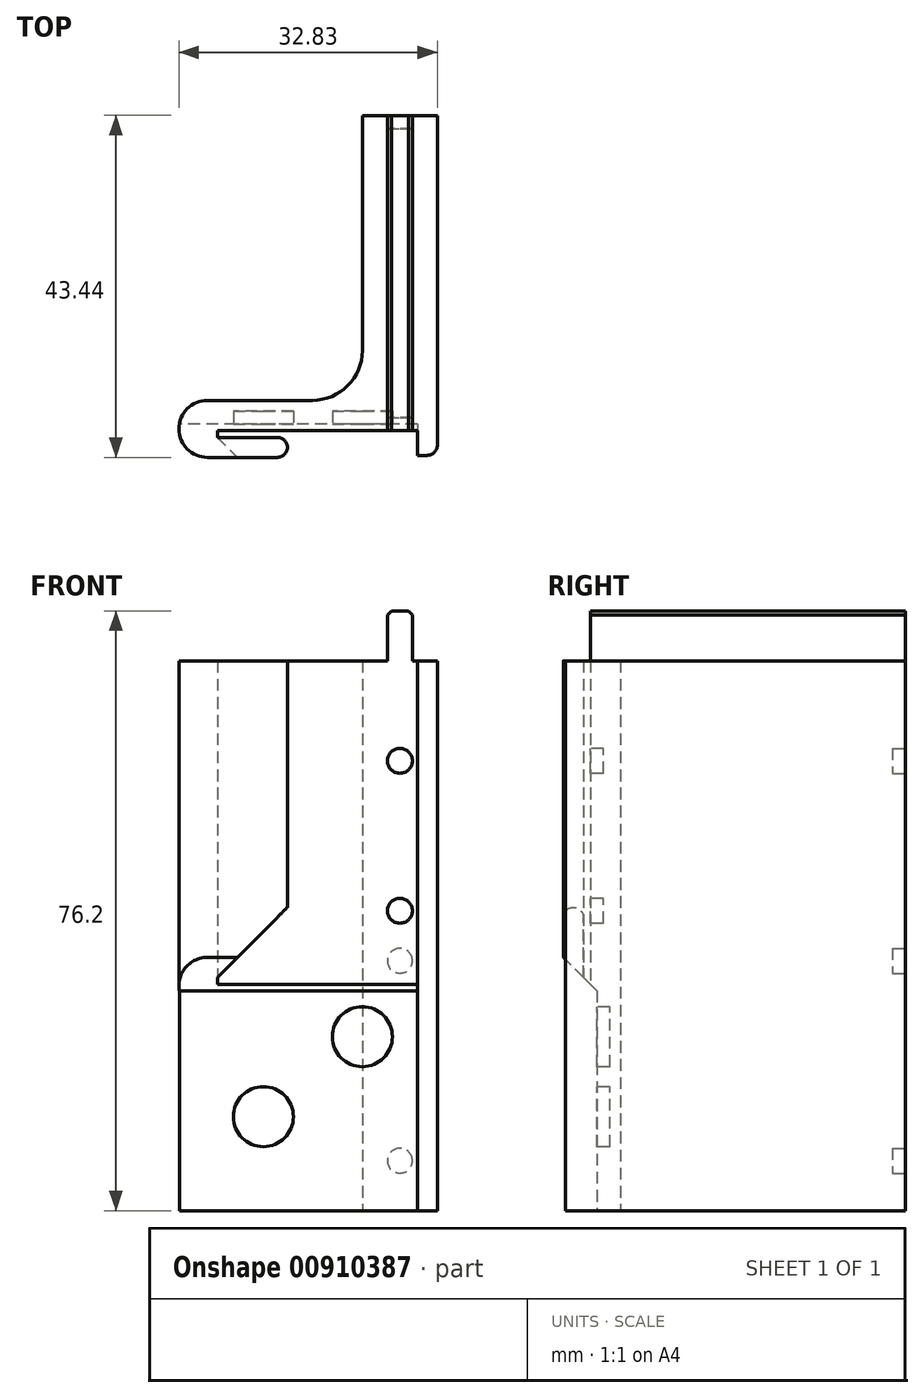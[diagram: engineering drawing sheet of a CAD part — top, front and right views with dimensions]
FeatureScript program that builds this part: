
annotation { "Feature Type Name" : "Feature", "Feature Type Description" : "" }
export const myFeature = defineFeature(function(context is Context, id is Id, definition is map)
    precondition{}
    {
        {
            var Q0;
            Q0=qCreatedBy(makeId("Top.planeOp"),FACE);
            var sketch = newSketch(context, id + "F0", { "sketchPlane" : qUnion([Q0])});
            skLineSegment(sketch, "E0", {"start": v(-6.99, 40) * mm, "end": v(-6.99, 10.16) * mm});
            skLineSegment(sketch, "E1", {"start": v(-13.34, 3.8) * mm, "end": v(-26.67, 3.8) * mm});
            skLineSegment(sketch, "E2", {"start": v(-26.67, -3.43) * mm, "end": v(-17.78, -3.43) * mm});
            skLineSegment(sketch, "E3", {"start": v(-17.78, -0.89) * mm, "end": v(-25.4, -0.89) * mm});
            skLineSegment(sketch, "E4", {"start": v(-25.4, -0.89) * mm, "end": v(-25.4, 0) * mm});
            skLineSegment(sketch, "E5", {"start": v(-25.4, 0) * mm, "end": v(0, 0) * mm});
            skLineSegment(sketch, "E6", {"start": v(0, 0) * mm, "end": v(0, -3.18) * mm});
            skLineSegment(sketch, "E7", {"start": v(0, -3.18) * mm, "end": v(1.22, -3.18) * mm});
            skLineSegment(sketch, "E8", {"start": v(2.54, -1.85) * mm, "end": v(2.54, 40) * mm});
            skLineSegment(sketch, "E9", {"start": v(2.54, 40) * mm, "end": v(-6.99, 40) * mm});
            skArc(sketch, "E10", {"start": v(-26.67, 3.8) * mm, "mid": v(-30.29, 0.2) * mm, "end": v(-26.67, -3.43) * mm});
            skPoint(sketch, "E11.visualSharp", {"position": v(-6.99, 3.81) * mm});
            skArc(sketch, "E11.filletArc", {"start": v(-13.34, 3.8) * mm, "mid": v(-8.84, 5.67) * mm, "end": v(-6.99, 10.16) * mm});
            skPoint(sketch, "E12.visualSharp", {"position": v(2.54, -3.18) * mm});
            skArc(sketch, "E12.filletArc", {"start": v(1.22, -3.18) * mm, "mid": v(2.15, -2.79) * mm, "end": v(2.54, -1.85) * mm});
            skArc(sketch, "E13", {"start": v(-17.78, -3.43) * mm, "mid": v(-16.51, -2.16) * mm, "end": v(-17.78, -0.89) * mm});
            skSolve(sketch);
        }
        {
            var Q0;
            Q0=qSketchRegion(id+"F0",true);
            extrude(context, id + "F1", {"entities" : qUnion([Q0]), "depth" : 69.85 * mm, "offsetDistance" : 25.4 * mm});
        }
        {
            var Q0;
            Q0=makeQuery(id+"F1.opExtrude","SWEPT_FACE",FACE,{"disambiguationData":[OSD([sQuery(id+"F0.wireOp",EDGE,"E9")])]});
            var sketch = newSketch(context, id + "F2", { "sketchPlane" : qUnion([Q0])});
            skLineSegment(sketch, "E14.bottom", {"start": v(3.81, 69.85) * mm, "end": v(0.64, 69.85) * mm});
            skLineSegment(sketch, "E14.top", {"start": v(3.81, 76.2) * mm, "end": v(0.64, 76.2) * mm});
            skLineSegment(sketch, "E14.left", {"start": v(3.81, 69.85) * mm, "end": v(3.81, 76.2) * mm});
            skLineSegment(sketch, "E14.right", {"start": v(0.64, 69.85) * mm, "end": v(0.64, 76.2) * mm});
            skLineSegment(sketch, "E15", {"start": v(2.22, 69.85) * mm, "end": v(2.22, 0) * mm, "construction": true});
            skSolve(sketch);
        }
        {
            var Q0;
            Q0=qSketchRegion(id+"F2",true);
            var Q1;
            Q1=makeQuery(id+"F1.opExtrude","SWEPT_FACE",FACE,{"disambiguationData":[OSD([sQuery(id+"F0.wireOp",EDGE,"E5")])]});
            extrude(context, id + "F3", {"entities" : qUnion([Q0]), "operationType" : NewBodyOperationType.ADD, "endBound" : BoundingType.UP_TO_SURFACE, "oppositeDirection" : true, "depth" : 25.4 * mm, "endBoundEntityFace" : qUnion([Q1]), "offsetDistance" : 25.4 * mm});
        }
        {
            var Q0;
            Q0=makeQuery(id+"FGGUkSzP3J2FlrJ_1.boolean.opBoolean","COPY",EDGE,{"derivedFrom":makeQuery(id+"FGGUkSzP3J2FlrJ_1.opExtrude","SWEPT_EDGE",EDGE,{"disambiguationData":[OSD([sQuery(id+"F0.wireOp",EDGE,"E9"),sQuery(id+"FaeWGxnTma6XmSR_1.wireOp",EDGE,"7cqQJsnl-rrB4-1SHC-6Jgg-oraov4HQkfV0.bottom"),sQuery(id+"FaeWGxnTma6XmSR_1.wireOp",EDGE,"7cqQJsnl-rrB4-1SHC-6Jgg-oraov4HQkfV0.right")])]})});
            var Q1;
            Q1=makeQuery(id+"FGGUkSzP3J2FlrJ_1.boolean.opBoolean","COPY",EDGE,{"derivedFrom":makeQuery(id+"FGGUkSzP3J2FlrJ_1.opExtrude","SWEPT_EDGE",EDGE,{"disambiguationData":[OSD([sQuery(id+"F0.wireOp",EDGE,"E9"),sQuery(id+"FaeWGxnTma6XmSR_1.wireOp",EDGE,"7cqQJsnl-rrB4-1SHC-6Jgg-oraov4HQkfV0.bottom"),sQuery(id+"FaeWGxnTma6XmSR_1.wireOp",EDGE,"7cqQJsnl-rrB4-1SHC-6Jgg-oraov4HQkfV0.left")])]})});
            var Q2;
            Q2=makeQuery(id+"F3.opExtrude","SWEPT_EDGE",EDGE,{"disambiguationData":[OSD([sQuery(id+"F2.wireOp",EDGE,"E14.top"),sQuery(id+"F2.wireOp",EDGE,"E14.right")])]});
            var Q3;
            Q3=makeQuery(id+"F3.opExtrude","SWEPT_EDGE",EDGE,{"disambiguationData":[OSD([sQuery(id+"F2.wireOp",EDGE,"E14.top"),sQuery(id+"F2.wireOp",EDGE,"E14.left")])]});
            chamfer(context, id + "F4", {"entities" : qUnion([Q0, Q1, Q2, Q3]), "width" : 0.5 * mm, "tangentPropagation" : true});
        }
        {
            var Q0;
            Q0=makeQuery(id+"F3.boolean.opBoolean","MERGE",FACE,{"derivedFrom":[makeQuery(id+"F1.opExtrude","SWEPT_FACE",FACE,{"disambiguationData":[OSD([sQuery(id+"F0.wireOp",EDGE,"E9")])]}),makeQuery(id+"F3.opExtrude","CAP_FACE",FACE,{"disambiguationData":[OSD([sQuery(id+"F2.wireOp",EDGE,"E14.bottom"),sQuery(id+"F2.wireOp",EDGE,"E14.top"),sQuery(id+"F2.wireOp",EDGE,"E14.left"),sQuery(id+"F2.wireOp",EDGE,"E14.right")])],"isStart":true})]});
            var sketch = newSketch(context, id + "F5", { "sketchPlane" : qUnion([Q0])});
            skCircle(sketch, "E16", {"center": v(2.22, 6.35) * mm, "radius": 1.59 * mm});
            skCircle(sketch, "E17", {"center": v(2.22, 31.75) * mm, "radius": 1.59 * mm});
            skCircle(sketch, "E18", {"center": v(2.22, 57.15) * mm, "radius": 1.59 * mm});
            skLineSegment(sketch, "E19", {"start": v(2.22, 0) * mm, "end": v(2.22, 6.35) * mm, "construction": true});
            skLineSegment(sketch, "E20", {"start": v(2.22, 31.75) * mm, "end": v(2.22, 6.35) * mm, "construction": true});
            skLineSegment(sketch, "E21", {"start": v(2.22, 57.15) * mm, "end": v(2.22, 31.75) * mm, "construction": true});
            skLineSegment(sketch, "E22", {"start": v(2.22, 57.15) * mm, "end": v(2.22, 69.85) * mm, "construction": true});
            skSolve(sketch);
        }
        {
            var Q0;
            Q0=qSketchRegion(id+"F5",true);
            extrude(context, id + "F6", {"entities" : qUnion([Q0]), "operationType" : NewBodyOperationType.REMOVE, "oppositeDirection" : true, "depth" : 1.65 * mm, "offsetDistance" : 25.4 * mm});
        }
        {
            var Q0;
            Q0=makeQuery(id+"F3.boolean.opBoolean","MERGE",FACE,{"derivedFrom":[makeQuery(id+"F1.opExtrude","SWEPT_FACE",FACE,{"disambiguationData":[OSD([sQuery(id+"F0.wireOp",EDGE,"E5")])]}),makeQuery(id+"F3.opExtrude","CAP_FACE",FACE,{"disambiguationData":[OSD([sQuery(id+"F2.wireOp",EDGE,"E14.bottom"),sQuery(id+"F2.wireOp",EDGE,"E14.top"),sQuery(id+"F2.wireOp",EDGE,"E14.left"),sQuery(id+"F2.wireOp",EDGE,"E14.right")])],"isStart":false})]});
            var sketch = newSketch(context, id + "F7", { "sketchPlane" : qUnion([Q0])});
            skCircle(sketch, "E23.2.0", {"center": v(-2.22, 57.15) * mm, "radius": 1.59 * mm});
            skCircle(sketch, "E24", {"center": v(-2.22, 38.1) * mm, "radius": 1.59 * mm});
            skLineSegment(sketch, "E25", {"start": v(-2.22, 57.15) * mm, "end": v(-2.22, 38.1) * mm, "construction": true});
            skSolve(sketch);
        }
        {
            var Q0;
            Q0=qSketchRegion(id+"F7",true);
            extrude(context, id + "F8", {"entities" : qUnion([Q0]), "operationType" : NewBodyOperationType.REMOVE, "oppositeDirection" : true, "depth" : 1.65 * mm, "offsetDistance" : 25.4 * mm});
        }
        {
            var Q0;
            Q0=makeQuery(id+"F1.opExtrude","CAP_FACE",FACE,{"disambiguationData":[OSD([sQuery(id+"F0.wireOp",EDGE,"E0"),sQuery(id+"F0.wireOp",EDGE,"E1"),sQuery(id+"F0.wireOp",EDGE,"E2"),sQuery(id+"F0.wireOp",EDGE,"E3"),sQuery(id+"F0.wireOp",EDGE,"E4"),sQuery(id+"F0.wireOp",EDGE,"E5"),sQuery(id+"F0.wireOp",EDGE,"E6"),sQuery(id+"F0.wireOp",EDGE,"E7"),sQuery(id+"F0.wireOp",EDGE,"E8"),sQuery(id+"F0.wireOp",EDGE,"E9"),sQuery(id+"F0.wireOp",EDGE,"E10"),sQuery(id+"F0.wireOp",EDGE,"E11.filletArc"),sQuery(id+"F0.wireOp",EDGE,"E12.filletArc"),sQuery(id+"F0.wireOp",EDGE,"E13")])],"isStart":true});
            var sketch = newSketch(context, id + "F9", { "sketchPlane" : qUnion([Q0])});
            skLineSegment(sketch, "E26.bottom", {"start": v(0, -0.81) * mm, "end": v(-30.29, -0.81) * mm});
            skLineSegment(sketch, "E26.top", {"start": v(0, 3.43) * mm, "end": v(-30.29, 3.43) * mm});
            skLineSegment(sketch, "E26.left", {"start": v(0, -0.81) * mm, "end": v(0, 3.43) * mm});
            skLineSegment(sketch, "E26.right", {"start": v(-30.29, -0.81) * mm, "end": v(-30.29, 3.43) * mm});
            skSolve(sketch);
        }
        {
            var Q0;
            Q0 = qSketchRegion(id + "F9", true);
            extrude(context, id + "F10", {"entities" : qUnion([Q0]), "operationType" : NewBodyOperationType.REMOVE, "oppositeDirection" : true, "depth" : 27.94 * mm, "offsetDistance" : 25.4 * mm});
        }
        {
            var Q0;
            Q0=makeQuery(id+"F10.boolean.opBoolean","COPY",FACE,{"derivedFrom":makeQuery(id+"F10.opExtrude","SWEPT_FACE",FACE,{"disambiguationData":[OSD([sQuery(id+"F9.wireOp",EDGE,"E26.bottom")])]})});
            var sketch = newSketch(context, id + "F11", { "sketchPlane" : qUnion([Q0])});
            skCircle(sketch, "E27", {"center": v(-6.99, 22.1) * mm, "radius": 3.81 * mm});
            skCircle(sketch, "E28", {"center": v(-19.56, 11.94) * mm, "radius": 3.81 * mm});
            skSolve(sketch);
        }
        {
            var Q0;
            Q0 = qSketchRegion(id + "F11", true);
            extrude(context, id + "F12", {"entities" : qUnion([Q0]), "operationType" : NewBodyOperationType.REMOVE, "oppositeDirection" : true, "depth" : 1.65 * mm, "offsetDistance" : 25.4 * mm});
        }
        {
            var Q0;
            Q0=makeQuery(id+"F10.boolean.opBoolean","MERGE",FACE,{"derivedFrom":[makeQuery(id+"F1.opExtrude","SWEPT_FACE",FACE,{"disambiguationData":[OSD([sQuery(id+"F0.wireOp",EDGE,"E6")])]})],"fromTools":[makeQuery(id+"F10.opExtrude","SWEPT_FACE",FACE,{"disambiguationData":[OSD([sQuery(id+"F9.wireOp",EDGE,"E26.left")])]})]});
            var sketch = newSketch(context, id + "F13", { "sketchPlane" : qUnion([Q0])});
            skLineSegment(sketch, "E29", {"start": v(-0.81, 27.94) * mm, "end": v(3.43, 32.18) * mm});
            skLineSegment(sketch, "E30", {"start": v(3.43, 27.94) * mm, "end": v(-0.81, 27.94) * mm});
            skLineSegment(sketch, "E31", {"start": v(3.43, 32.18) * mm, "end": v(3.43, 27.94) * mm});
            skSolve(sketch);
        }
        {
            var Q0;
            Q0 = qSketchRegion(id + "F13", true);
            extrude(context, id + "F14", {"entities" : qUnion([Q0]), "operationType" : NewBodyOperationType.REMOVE, "endBound" : BoundingType.THROUGH_ALL, "depth" : 25.4 * mm, "offsetDistance" : 25.4 * mm});
        }
        {
            var Q0;
            Q0=makeQuery(id+"F1.opExtrude","SWEPT_FACE",FACE,{"disambiguationData":[OSD([sQuery(id+"F0.wireOp",EDGE,"E2")])]});
            var sketch = newSketch(context, id + "F15", { "sketchPlane" : qUnion([Q0])});
            skLineSegment(sketch, "E32", {"start": v(-25.4, 29.64) * mm, "end": v(-12.7, 29.64) * mm});
            skLineSegment(sketch, "E33", {"start": v(-12.7, 29.64) * mm, "end": v(-12.7, 42.34) * mm});
            skLineSegment(sketch, "E34", {"start": v(-12.7, 42.34) * mm, "end": v(-25.4, 29.64) * mm});
            skSolve(sketch);
        }
        {
            var Q0;
            Q0 = qSketchRegion(id + "F15", true);
            var Q1;
            Q1=makeQuery(id+"F1.opExtrude","SWEPT_FACE",FACE,{"disambiguationData":[OSD([sQuery(id+"F0.wireOp",EDGE,"E3")])]});
            extrude(context, id + "F16", {"entities" : qUnion([Q0]), "operationType" : NewBodyOperationType.REMOVE, "endBound" : BoundingType.UP_TO_SURFACE, "oppositeDirection" : true, "depth" : 25.4 * mm, "endBoundEntityFace" : qUnion([Q1]), "offsetDistance" : 25.4 * mm});
        }
    });
